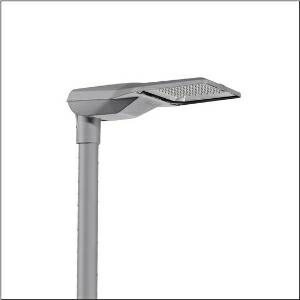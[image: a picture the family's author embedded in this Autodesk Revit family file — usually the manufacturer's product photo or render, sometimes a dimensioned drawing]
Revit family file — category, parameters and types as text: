
# Revit family: streetlight_sl_21_iq_midi___st0_5a_5xe3b41g08mb_6195
name_source: partatom
category: Lighting Fixtures
units: mm (PartAtom-declared; Revit-internal decimal feet)

## family parameters
Cut with Voids When Loaded = No
Host = Face
Light Source = No
Part Type = Normal
Room Calculation Point = No
Round Connector Dimension = Use Diameter
Shared = No

## types (1)
- --- (1 x LED, 20360 lm, 146.7 W, 4000K)
    Apparent Load = 147 VA
    CIE Flux Codes = 41 75 97 100 100
    Color Rendering = 70
    Color Temperature = 4000K
    Default Elevation = 1800 mm
    Description = Streetlight SL 21 iQ midi, mast luminaire, primary light control with lens, of PMMA, primary optical cover: cover, of toughened safety glass, transparent, light distribution: ST0.5a, light emission: direct distribution, primary light characteristic: asymmetric, installation type: post-top, side-entry, LED, High Power LED, rated luminous flux: 20.360lm, luminous efficacy: 139lm/W, light colour: 740, colour temperature: 4000K, control gear: iQ Street-Remote, control: Street-Remote, Auto-Match, Temp-Guard, Lumen-Switch, Night-Set, Smart-Wire, Light-Fading, Desk-Remote (wireless, voltage-free reading and setting of iQ features in the workshop via application-optimized NFC function/RFID function), optimised constant luminous flux control (CLO 2.0), pre-setting: linear dimming characteristic, mains connection: 230..240V, AC, 50/60Hz, start of lifetime: 147W, end of service life: 161W, reduction: 62W, luminaire housing, of diecast aluminium, powder-coated, Siteco® metallic grey (DB 702S), corrosivity category C5 mid according to DIN EN ISO 12944, please order mast flange separately, inclination adjustable: 0°, 5°, 10°, 15°, sealing non-destructively replaceable, multi-level sealing system, length: 644mm, width: 335mm, height: 110mm, mast flange for spigot size: 42mm (side-entry): 5XC10008XM4, 60/48mm (side-entry/post-top): 5XC10108XM2, 76/60mm (side-entry/post-top): 5XC10108XM1, mounting height: 4..8m, protection rating (complete): IP66, insulation class (complete): insulation class II (safety insulation), certification: CE, ENEC, ENEC+, VDE, impact resistance: IK10, permissible operating ambient temperature for outdoor applications: -40..+50°C, standard-compliant lighting for roads and squares, packaging unit: 1 piece

Light Distribution: ST0.5a
    Height = 111 mm
    Lamp = 1 x LED
    Lamp Light Flux = 20360 lm
    Lamp Power = 146.7 W
    Lamp count = 1
    Length = 644 mm
    Luminous efficacy = 139 lm/W
    Manufacturer = Siteco
    ModVariant = No
    Model = 5XE3B41G08MB
    Number of Poles = 1
    OnlyDefault = Yes
    Power Factor = 1
    Product Name = Streetlight SL 21 iQ midi | ST0.5a
    Product group = mast luminaire | pylon top
    ProductGroupID = 6100
    Protection Class = Protection class II
    Protection Degree = IP 66
    RLX_Detail_Level = 1
    RLX_Emergency_Light_Flux = 0 lm
    RLX_Emergency_Type = 0
    RLX_Emergency_Type_DB = No
    RlxData = <blob elided: 37821 chars, md5=7f1efb68>
    Socket = socket
    Standby Power = 0 W
    System Light Flux = 20360 lm
    System Power = 147 W
    Type Comments = factory setting: luminous flux: 100 % | dim-lin: 254 | 753 mA
    Type Image = l_1004298.jpg
    URL = http://relux.com
    VarID = @adj_213059
    Voltage = 0 V
    Weight = 0.00 kg
    Width = 336 mm

## geometry (parser evidence)
native form markers: Blend x4, Sweep x10
no freeform markers — native parametric forms only
